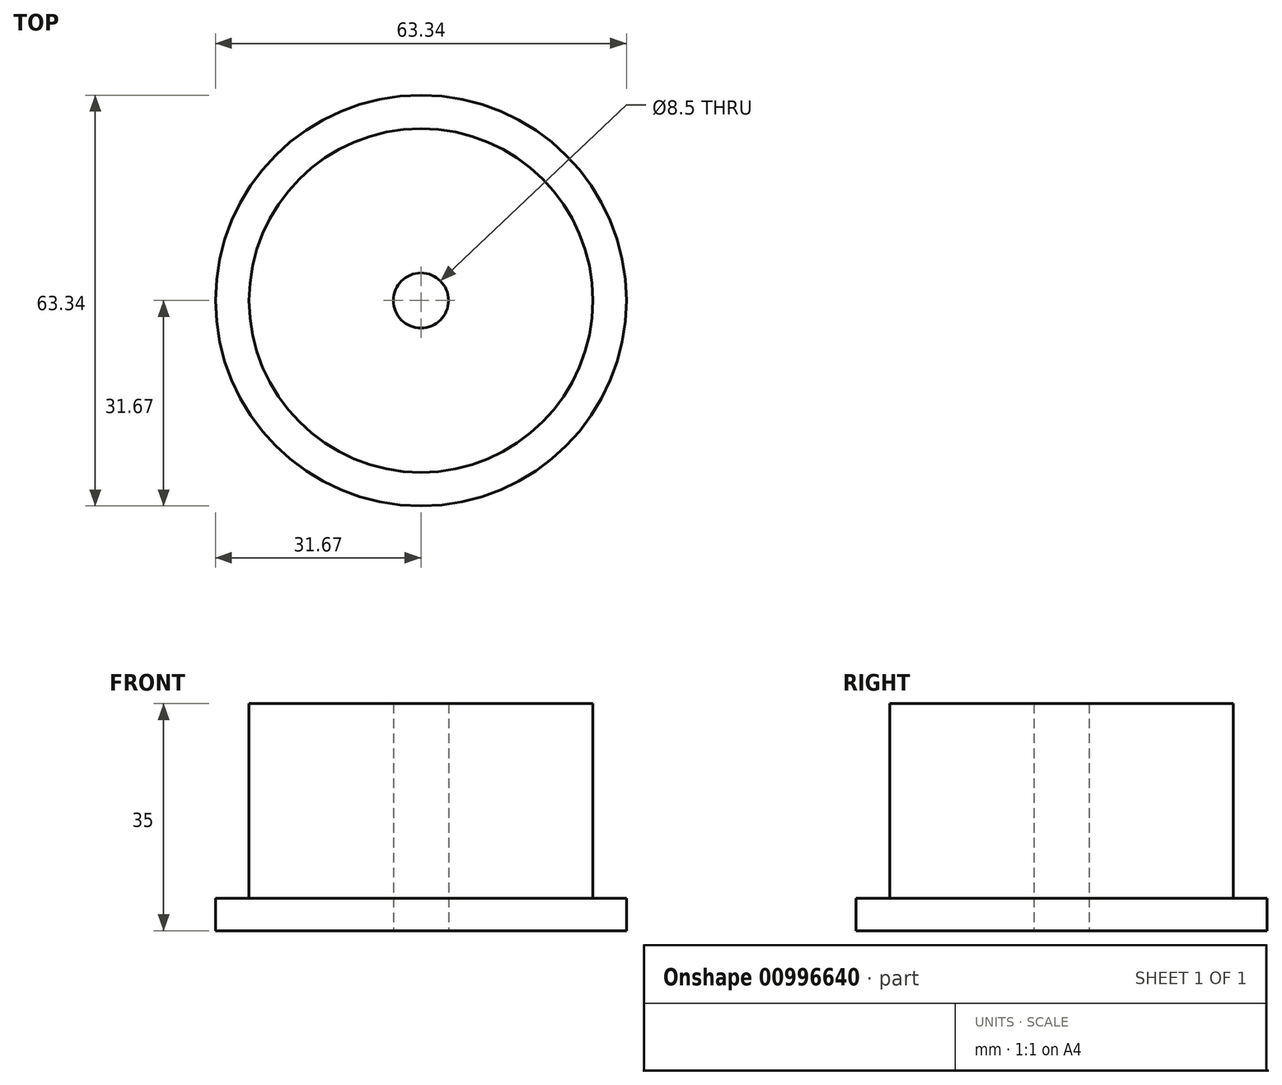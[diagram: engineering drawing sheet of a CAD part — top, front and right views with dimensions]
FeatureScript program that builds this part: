
annotation { "Feature Type Name" : "Feature", "Feature Type Description" : "" }
export const myFeature = defineFeature(function(context is Context, id is Id, definition is map)
    precondition{}
    {
        {
            var Q0;
            Q0=qCreatedBy(makeId("Top.planeOp"),FACE);
            var sketch = newSketch(context, id + "F0", { "sketchPlane" : qUnion([Q0])});
            skCircle(sketch, "E0", {"center": v(0, 0) * mm, "radius": 26.5 * mm});
            skCircle(sketch, "E1", {"center": v(0, 0) * mm, "radius": 31.67 * mm});
            skSolve(sketch);
        }
        {
            var Q0;
            Q0=makeQuery(id+"F0.imprint","IMPRINT",FACE,{"disambiguationData":[TD([[makeQuery(id+"F0.imprint","IMPRINT",EDGE,{"derivedFrom":sQuery(id+"F0.wireOp",EDGE,"E0")}),1.0]])]});
            extrude(context, id + "F1", {"entities" : qUnion([Q0]), "depth" : 35 * mm, "offsetDistance" : 25.4 * mm});
        }
        {
            var Q0;
            Q0=makeQuery(id+"F0.imprint","IMPRINT",FACE,{"disambiguationData":[TD([[makeQuery(id+"F0.imprint","IMPRINT",EDGE,{"derivedFrom":sQuery(id+"F0.wireOp",EDGE,"E0")}),-1.0]])]});
            extrude(context, id + "F2", {"entities" : qUnion([Q0]), "operationType" : NewBodyOperationType.ADD, "depth" : 5 * mm, "offsetDistance" : 25.4 * mm});
        }
        {
            var Q0;
            Q0=sQuery(id+"F0.wireOp",VERTEX,"E0.center");
            var Q1;
            Q1=makeQuery(id+"F1.opExtrude","SWEPT_BODY",BODY,{"disambiguationData":[OSD([sQuery(id+"F0.wireOp",EDGE,"E0")])]});
            hole(context, id + "F3", {"style" : HoleStyle.SIMPLE, "endStyle" : HoleEndStyle.THROUGH, "oppositeDirection" : true, "holeDiameter" : 8.5 * mm, "majorDiameter" : 6.35 * mm, "isTappedThrough" : true, "tappedDepth" : 12.7 * mm, "tapClearance" : 3, "locations" : qUnion([Q0]), "scope" : qUnion([Q1])});
        }
    });
